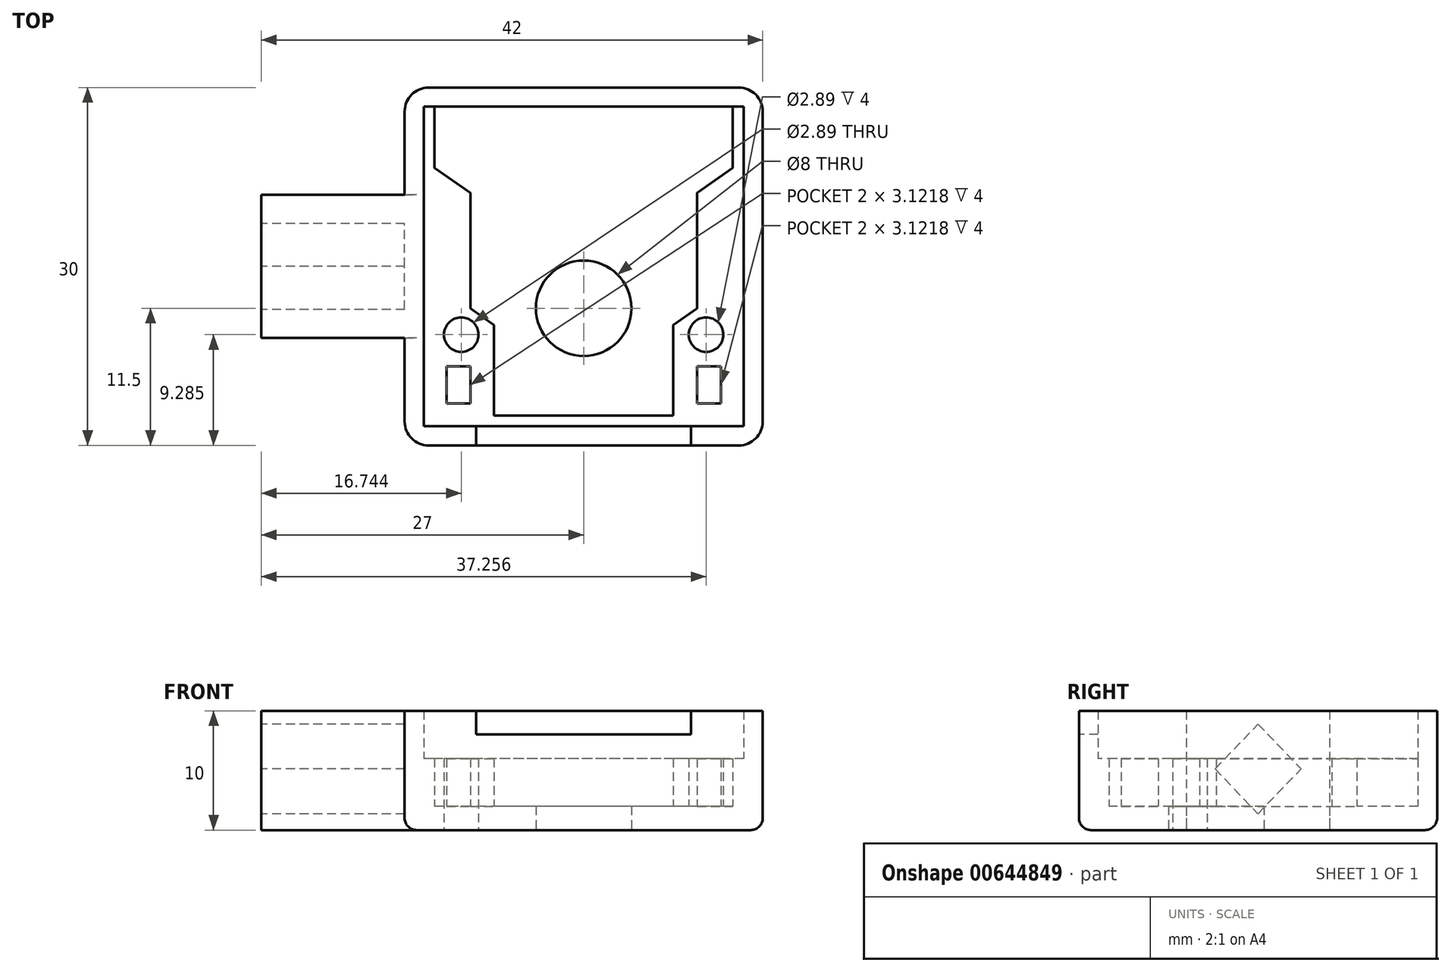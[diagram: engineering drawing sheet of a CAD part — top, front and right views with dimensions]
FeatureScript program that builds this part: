
annotation { "Feature Type Name" : "Feature", "Feature Type Description" : "" }
export const myFeature = defineFeature(function(context is Context, id is Id, definition is map)
    precondition{}
    {
        {
            var Q0;
            Q0=qCreatedBy(makeId("Top.planeOp"),FACE);
            var sketch = newSketch(context, id + "F0", { "sketchPlane" : qUnion([Q0])});
            skLineSegment(sketch, "E0.bottom", {"start": v(15, 15) * mm, "end": v(-15, 15) * mm});
            skLineSegment(sketch, "E0.top", {"start": v(15, -15) * mm, "end": v(-15, -15) * mm});
            skLineSegment(sketch, "E0.left", {"start": v(15, 15) * mm, "end": v(15, -15) * mm});
            skLineSegment(sketch, "E0.right", {"start": v(-15, 15) * mm, "end": v(-15, -15) * mm});
            skPoint(sketch, "E0.middle", {"position": v(0, 0) * mm});
            skLineSegment(sketch, "E1.bottom", {"start": v(13.4, 13.4) * mm, "end": v(-13.4, 13.4) * mm});
            skLineSegment(sketch, "E1.top", {"start": v(13.4, -13.4) * mm, "end": v(-13.4, -13.4) * mm});
            skLineSegment(sketch, "E1.left", {"start": v(13.4, 13.4) * mm, "end": v(13.4, -13.4) * mm});
            skLineSegment(sketch, "E1.right", {"start": v(-13.4, 13.4) * mm, "end": v(-13.4, -13.4) * mm});
            skLineSegment(sketch, "E2.bottom", {"start": v(12.5, 12.5) * mm, "end": v(-12.5, 12.5) * mm});
            skLineSegment(sketch, "E2.top", {"start": v(12.5, -12.5) * mm, "end": v(-12.5, -12.5) * mm});
            skLineSegment(sketch, "E2.left", {"start": v(12.5, 12.5) * mm, "end": v(12.5, -12.5) * mm});
            skLineSegment(sketch, "E2.right", {"start": v(-12.5, 12.5) * mm, "end": v(-12.5, -12.5) * mm});
            skCircle(sketch, "E3", {"center": v(0, -3.5) * mm, "radius": 4 * mm});
            skPoint(sketch, "E3.centerSnap0", {"position": v(0, 15) * mm});
            skLineSegment(sketch, "E4", {"start": v(-12.5, -1.4) * mm, "end": v(-7.5, -4.9) * mm});
            skLineSegment(sketch, "E5", {"start": v(-7.5, -4.9) * mm, "end": v(-7.5, -12.5) * mm});
            skLineSegment(sketch, "E6.MirrorCS", {"start": v(7.5, -4.9) * mm, "end": v(7.5, -12.5) * mm});
            skLineSegment(sketch, "E7.MirrorCS", {"start": v(12.5, -1.4) * mm, "end": v(7.5, -4.9) * mm});
            skLineSegment(sketch, "E8", {"start": v(-9.5, -3.5) * mm, "end": v(-9.5, 6.17) * mm});
            skLineSegment(sketch, "E9", {"start": v(-9.5, 6.17) * mm, "end": v(-12.5, 8.27) * mm});
            skLineSegment(sketch, "E10.MirrorCS", {"start": v(9.5, -3.5) * mm, "end": v(9.5, 6.17) * mm});
            skLineSegment(sketch, "E11.MirrorCS", {"start": v(9.5, 6.17) * mm, "end": v(12.5, 8.27) * mm});
            skLineSegment(sketch, "E12", {"start": v(-12.5, 12.5) * mm, "end": v(-12.5, 13.4) * mm});
            skLineSegment(sketch, "E13", {"start": v(12.5, 12.5) * mm, "end": v(12.5, 13.4) * mm});
            skLineSegment(sketch, "E14.bottom", {"start": v(-15, 6) * mm, "end": v(-27, 6) * mm});
            skLineSegment(sketch, "E14.top", {"start": v(-15, -6) * mm, "end": v(-27, -6) * mm});
            skLineSegment(sketch, "E14.left", {"start": v(-15, 6) * mm, "end": v(-15, -6) * mm});
            skLineSegment(sketch, "E14.right", {"start": v(-27, 6) * mm, "end": v(-27, -6) * mm});
            skCircle(sketch, "E15", {"center": v(10.26, -5.72) * mm, "radius": 1.45 * mm});
            skLineSegment(sketch, "E16.bottom", {"start": v(11.5, -11.48) * mm, "end": v(9.5, -11.48) * mm});
            skLineSegment(sketch, "E16.top", {"start": v(11.5, -8.36) * mm, "end": v(9.5, -8.36) * mm});
            skLineSegment(sketch, "E16.left", {"start": v(11.5, -11.48) * mm, "end": v(11.5, -8.36) * mm});
            skLineSegment(sketch, "E16.right", {"start": v(9.5, -11.48) * mm, "end": v(9.5, -8.36) * mm});
            skLineSegment(sketch, "E17.MirrorCS", {"start": v(-11.5, -11.48) * mm, "end": v(-11.5, -8.36) * mm});
            skLineSegment(sketch, "E18.MirrorCS", {"start": v(-11.5, -8.36) * mm, "end": v(-9.5, -8.36) * mm});
            skLineSegment(sketch, "E19.MirrorCS", {"start": v(-9.5, -11.48) * mm, "end": v(-9.5, -8.36) * mm});
            skLineSegment(sketch, "E20.MirrorCS", {"start": v(-11.5, -11.48) * mm, "end": v(-9.5, -11.48) * mm});
            skCircle(sketch, "E21.MirrorC", {"center": v(-10.26, -5.72) * mm, "radius": 1.45 * mm});
            skSolve(sketch);
        }
        {
            var Q0;
            Q0=makeQuery(id+"F0.imprint","IMPRINT",FACE,{"disambiguationData":[TD([[makeQuery(id+"F0.imprint","IMPRINT",EDGE,{"derivedFrom":sQuery(id+"F0.wireOp",EDGE,"E0.bottom")}),1.0]])]});
            var Q1;
            Q1=makeQuery(id+"F0.imprint","IMPRINT",FACE,{"disambiguationData":[TD([[makeQuery(id+"F0.imprint","IMPRINT",EDGE,{"derivedFrom":sQuery(id+"F0.wireOp",EDGE,"E14.bottom")}),1.0]])]});
            extrude(context, id + "F1", {"entities" : qUnion([Q0, Q1]), "depth" : 10 * mm, "offsetDistance" : 25 * mm});
        }
        {
            var Q0;
            {var subQ0=sQuery(id+"F0.wireOp",EDGE,"E5");Q0=makeQuery(id+"F0.imprint","IMPRINT",FACE,{"disambiguationData":[TD([[makeQuery(id+"F0.imprint","IMPRINT",EDGE,{"derivedFrom":subQ0}),-1.0]])]});}
            var Q1;
            {var subQ4=sQuery(id+"F0.wireOp",EDGE,"E8");Q1=makeQuery(id+"F0.imprint","IMPRINT",FACE,{"disambiguationData":[TD([[makeQuery(id+"F0.imprint","IMPRINT",EDGE,{"derivedFrom":subQ4}),1.0]])]});}
            var Q2;
            {var subQ0=sQuery(id+"F0.wireOp",EDGE,"E10.MirrorCS");Q2=makeQuery(id+"F0.imprint","IMPRINT",FACE,{"disambiguationData":[TD([[makeQuery(id+"F0.imprint","IMPRINT",EDGE,{"derivedFrom":subQ0}),-1.0]])]});}
            var Q3;
            {var subQ6=sQuery(id+"F0.wireOp",EDGE,"E6.MirrorCS");Q3=makeQuery(id+"F0.imprint","IMPRINT",FACE,{"disambiguationData":[TD([[makeQuery(id+"F0.imprint","IMPRINT",EDGE,{"derivedFrom":subQ6}),1.0]])]});}
            var Q4;
            Q4=makeQuery(id+"F0.imprint","IMPRINT",FACE,{"disambiguationData":[TD([[makeQuery(id+"F0.imprint","IMPRINT",EDGE,{"derivedFrom":sQuery(id+"F0.wireOp",EDGE,"E1.top")}),-1.0]])]});
            extrude(context, id + "F2", {"entities" : qUnion([Q0, Q1, Q2, Q3, Q4]), "operationType" : NewBodyOperationType.ADD, "depth" : 6 * mm, "offsetDistance" : 25 * mm});
        }
        {
            var Q0;
            Q0=makeQuery(id+"F0.imprint","IMPRINT",FACE,{"disambiguationData":[TD([[makeQuery(id+"F0.imprint","IMPRINT",EDGE,{"derivedFrom":sQuery(id+"F0.wireOp",EDGE,"ygr4CzvK-AAde-YyK9-W9yW-oeCBNqkHNDKr")}),1.0]])]});
            var Q1;
            Q1=makeQuery(id+"F0.imprint","IMPRINT",FACE,{"disambiguationData":[TD([[makeQuery(id+"F0.imprint","IMPRINT",EDGE,{"derivedFrom":sQuery(id+"F0.wireOp",EDGE,"79cd0a19-6e1c-441f-be4d-5e612219fc520.MirrorC")}),1.0]])]});
            var Q2;
            {var subQ5=sQuery(id+"F0.wireOp",EDGE,"E2.bottom");Q2=makeQuery(id+"F0.imprint","IMPRINT",FACE,{"disambiguationData":[TD([[makeQuery(id+"F0.imprint","IMPRINT",EDGE,{"derivedFrom":subQ5}),1.0]])]});}
            var Q3;
            Q3=makeQuery(id+"F0.imprint","IMPRINT",FACE,{"disambiguationData":[TD([[makeQuery(id+"F0.imprint","IMPRINT",EDGE,{"derivedFrom":sQuery(id+"F0.wireOp",EDGE,"E15")}),1.0]])]});
            var Q4;
            Q4=makeQuery(id+"F0.imprint","IMPRINT",FACE,{"disambiguationData":[TD([[makeQuery(id+"F0.imprint","IMPRINT",EDGE,{"derivedFrom":sQuery(id+"F0.wireOp",EDGE,"E16.bottom")}),-1.0]])]});
            var Q5;
            Q5=makeQuery(id+"F0.imprint","IMPRINT",FACE,{"disambiguationData":[TD([[makeQuery(id+"F0.imprint","IMPRINT",EDGE,{"derivedFrom":sQuery(id+"F0.wireOp",EDGE,"E17.MirrorCS")}),-1.0]])]});
            var Q6;
            Q6=makeQuery(id+"F0.imprint","IMPRINT",FACE,{"disambiguationData":[TD([[makeQuery(id+"F0.imprint","IMPRINT",EDGE,{"derivedFrom":sQuery(id+"F0.wireOp",EDGE,"E21.MirrorC")}),-1.0]])]});
            var Q7;
            Q7=makeQuery(id+"F0.imprint","IMPRINT",FACE,{"disambiguationData":[TD([[makeQuery(id+"F0.imprint","IMPRINT",EDGE,{"derivedFrom":sQuery(id+"F0.wireOp",EDGE,"E2.bottom")}),-1.0]])]});
            extrude(context, id + "F3", {"entities" : qUnion([Q0, Q1, Q2, Q3, Q4, Q5, Q6, Q7]), "operationType" : NewBodyOperationType.ADD, "depth" : 2 * mm, "offsetDistance" : 25 * mm});
        }
        {
            var Q0;
            Q0=makeQuery(id+"F1.opExtrude","SWEPT_FACE",FACE,{"disambiguationData":[OSD([sQuery(id+"F0.wireOp",EDGE,"E14.right")])]});
            var sketch = newSketch(context, id + "F4", { "sketchPlane" : qUnion([Q0])});
            skLineSegment(sketch, "E22.bottom", {"start": v(3.6, 5.12) * mm, "end": v(0, 8.87) * mm});
            skLineSegment(sketch, "E22.right", {"start": v(0, 8.87) * mm, "end": v(-3.6, 5.12) * mm});
            skLineSegment(sketch, "E23", {"start": v(-3.6, 5.12) * mm, "end": v(3.6, 5.12) * mm});
            skLineSegment(sketch, "E24.MirrorCS", {"start": v(0, 1.37) * mm, "end": v(-3.6, 5.12) * mm});
            skLineSegment(sketch, "E25.MirrorCS", {"start": v(3.6, 5.12) * mm, "end": v(0, 1.37) * mm});
            skSolve(sketch);
        }
        {
            var Q0;
            Q0=makeQuery(id+"F4.imprint","IMPRINT",FACE,{"disambiguationData":[TD([[makeQuery(id+"F4.imprint","IMPRINT",EDGE,{"derivedFrom":sQuery(id+"F4.wireOp",EDGE,"E22.bottom")}),1.0]])]});
            var Q1;
            Q1=makeQuery(id+"F4.imprint","IMPRINT",FACE,{"disambiguationData":[TD([[makeQuery(id+"F4.imprint","IMPRINT",EDGE,{"derivedFrom":sQuery(id+"F4.wireOp",EDGE,"E23")}),-1.0]])]});
            extrude(context, id + "F5", {"entities" : qUnion([Q0, Q1]), "operationType" : NewBodyOperationType.REMOVE, "oppositeDirection" : true, "depth" : 12 * mm, "offsetDistance" : 25 * mm});
        }
        {
            var Q0;
            Q0=makeQuery(id+"F1.opExtrude","SWEPT_EDGE",EDGE,{"disambiguationData":[OSD([sQuery(id+"F0.wireOp",EDGE,"E0.bottom"),sQuery(id+"F0.wireOp",EDGE,"E0.left")])]});
            var Q1;
            Q1=makeQuery(id+"F1.opExtrude","SWEPT_EDGE",EDGE,{"disambiguationData":[OSD([sQuery(id+"F0.wireOp",EDGE,"E0.bottom"),sQuery(id+"F0.wireOp",EDGE,"E0.right")])]});
            var Q2;
            Q2=makeQuery(id+"F1.opExtrude","SWEPT_EDGE",EDGE,{"disambiguationData":[OSD([sQuery(id+"F0.wireOp",EDGE,"E0.top"),sQuery(id+"F0.wireOp",EDGE,"E0.right")])]});
            var Q3;
            Q3=makeQuery(id+"F1.opExtrude","SWEPT_EDGE",EDGE,{"disambiguationData":[OSD([sQuery(id+"F0.wireOp",EDGE,"E0.top"),sQuery(id+"F0.wireOp",EDGE,"E0.left")])]});
            fillet(context, id + "F6", {"entities" : qUnion([Q0, Q1, Q2, Q3]), "radius" : 2 * mm, "tangentPropagation" : true, "allowEdgeOverflow" : false});
        }
        {
            var Q0;
            {var subQ0=sQuery(id+"F0.wireOp",EDGE,"E0.right");Q0=makeQuery(id+"F1.opExtrude","CAP_EDGE",EDGE,{"disambiguationData":[OSD([subQ0]),TDD([makeQuery(id+"F0.imprint","IMPRINT",EDGE,{"disambiguationData":[TD([[makeQuery(id+"F0.imprint","INTERSECT",VERTEX,{"derivedFrom":[sQuery(id+"F0.wireOp",EDGE,"E0.top"),subQ0]}),1.0]])],"derivedFrom":subQ0})])],"isStart":true});}
            var Q1;
            Q1=makeQuery(id+"F1.opExtrude","CAP_EDGE",EDGE,{"disambiguationData":[OSD([sQuery(id+"F0.wireOp",EDGE,"E0.top")])],"isStart":true});
            fillet(context, id + "F7", {"entities" : qUnion([Q0, Q1]), "radius" : 1 * mm, "tangentPropagation" : true, "allowEdgeOverflow" : false});
        }
        {
            var Q0;
            Q0=makeQuery(id+"F1.opExtrude","SWEPT_FACE",FACE,{"disambiguationData":[OSD([sQuery(id+"F0.wireOp",EDGE,"E0.top")])]});
            var sketch = newSketch(context, id + "F8", { "sketchPlane" : qUnion([Q0])});
            skLineSegment(sketch, "E26.bottom", {"start": v(-9, 10) * mm, "end": v(9, 10) * mm});
            skLineSegment(sketch, "E26.top", {"start": v(-9, 8) * mm, "end": v(9, 8) * mm});
            skLineSegment(sketch, "E26.left", {"start": v(-9, 10) * mm, "end": v(-9, 8) * mm});
            skLineSegment(sketch, "E26.right", {"start": v(9, 10) * mm, "end": v(9, 8) * mm});
            skSolve(sketch);
        }
        {
            var Q0;
            {var subQ0=sQuery(id+"F8.wireOp",EDGE,"E26.top");Q0=makeQuery(id+"F8.imprint","IMPRINT",FACE,{"disambiguationData":[TD([[makeQuery(id+"F8.imprint","IMPRINT",EDGE,{"derivedFrom":subQ0}),1.0]])]});}
            extrude(context, id + "F9", {"entities" : qUnion([Q0]), "operationType" : NewBodyOperationType.REMOVE, "oppositeDirection" : true, "depth" : 25 * mm, "offsetDistance" : 25 * mm});
        }
    });
